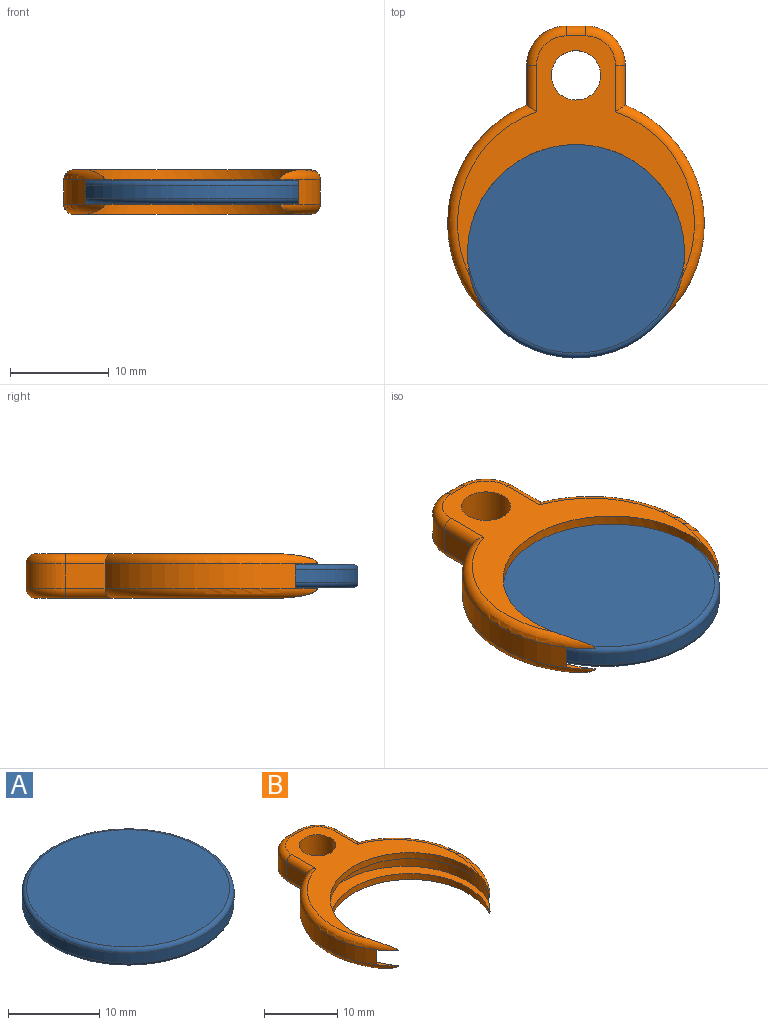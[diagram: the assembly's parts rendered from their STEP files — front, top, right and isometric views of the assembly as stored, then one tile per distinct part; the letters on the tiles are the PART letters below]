
ASSEMBLY  parts=2 mates=1
PART A: 277 faces, bbox 25.2x25.2x2.3 mm
  f0: plane 22.25x22.25mm, normal (0,0,-1), area 375.8mm2, adj f3,f5,f6,f7,f8,f23,f24,f25
  f1: cylinder r=11.62mm len=23.25mm, axis (0,0,-1), area 97.1mm2, adj f3,f4
  f2: plane 22.25x22.25mm, normal (0,0,1), area 388.8mm2, adj f4
  f3: torus R=11.12mm, axis (0,0,1), area 56.5mm2, adj f0,f1
  f4: torus R=11.12mm, axis (0,0,1), area 56.5mm2, adj f1,f2
  f5: plane 0.29x0.23mm, normal (0,-1,0), area 0.1mm2, adj f0,f6,f8,f9
  f6: plane 2.11x0.29mm, normal (-1,0,0), area 0.6mm2, adj f0,f5,f7,f9
  f7: plane 0.29x0.23mm, normal (0,1,0), area 0.1mm2, adj f0,f6,f8,f9
  f8: plane 2.11x0.29mm, normal (1,0,0), area 0.6mm2, adj f0,f5,f7,f9
  f9: plane 2.11x0.23mm, normal (0,0,-1), area 0.5mm2, adj f5,f6,f7,f8
  f10: extruded ~0.29x0.24mm, area 0.1mm2, adj f11,f53,f54,f273
  f11: extruded ~0.29x0.25mm, area 0.1mm2, adj f10,f12,f54,f273
  f12: extruded ~0.29x0.24mm, area 0.1mm2, adj f11,f13,f54,f273
  f13: extruded ~0.33x0.33mm, area 0.2mm2, adj f12,f14,f54,f273
  f14: extruded ~0.33x0.32mm, area 0.2mm2, adj f13,f53,f54,f273
  f15: extruded ~0.29x0.18mm, area 0.1mm2, adj f16,f51,f54,f55
  f16: extruded ~0.29x0.21mm, area 0.1mm2, adj f15,f17,f54,f55
  f17: extruded ~0.29x0.24mm, area 0.1mm2, adj f16,f18,f54,f55
  f18: plane 0.29x0.27mm, normal (0,-1,0), area 0.1mm2, adj f17,f19,f54,f55
  f19: extruded ~0.29x0.28mm, area 0.1mm2, adj f18,f20,f54,f55
  f20: extruded ~0.29x0.17mm, area 0.1mm2, adj f19,f21,f54,f55
  f21: extruded ~0.29x0.23mm, area 0.1mm2, adj f20,f22,f54,f55
  f22: extruded ~0.42x0.29mm, area 0.1mm2, adj f21,f51,f54,f55
  f23: plane 0.29x0.14mm, normal (-1,0,0), area 0mm2, adj f0,f24,f52,f54
  f24: plane 0.51x0.29mm, normal (0,1,0), area 0.2mm2, adj f0,f23,f25,f54
  f25: extruded ~0.29x0.21mm, area 0.1mm2, adj f0,f24,f26,f54
  f26: extruded ~0.41x0.29mm, area 0.1mm2, adj f0,f25,f27,f54
  f27: extruded ~0.38x0.29mm, area 0.1mm2, adj f0,f26,f28,f54
  f28: extruded ~0.29x0.26mm, area 0.1mm2, adj f0,f27,f29,f54
  f29: extruded ~0.29x0.19mm, area 0.1mm2, adj f0,f28,f30,f54
  f30: extruded ~0.29x0.14mm, area 0.1mm2, adj f0,f29,f31,f54
  f31: extruded ~0.29x0.14mm, area 0mm2, adj f0,f30,f32,f54
  f32: extruded ~0.29x0.13mm, area 0mm2, adj f0,f31,f33,f54
  f33: extruded ~0.29x0.1mm, area 0mm2, adj f0,f32,f34,f54
  f34: extruded ~0.29x0.24mm, area 0.1mm2, adj f0,f33,f35,f54
  f35: extruded ~0.29x0.23mm, area 0.1mm2, adj f0,f34,f36,f54
  f36: extruded ~0.31x0.29mm, area 0.1mm2, adj f0,f35,f37,f54
  f37: extruded ~0.45x0.29mm, area 0.1mm2, adj f0,f36,f38,f54
  f38: extruded ~0.58x0.29mm, area 0.2mm2, adj f0,f37,f39,f54
  f39: extruded ~0.38x0.29mm, area 0.1mm2, adj f0,f38,f40,f54
  f40: extruded ~0.3x0.29mm, area 0.1mm2, adj f0,f39,f41,f54
  f41: extruded ~0.37x0.29mm, area 0.1mm2, adj f0,f40,f42,f54
  f42: plane 0.29x0.26mm, normal (0,1,0), area 0.1mm2, adj f0,f41,f43,f54
  f43: extruded ~0.29x0.17mm, area 0.1mm2, adj f0,f42,f44,f54
  f44: extruded ~0.29x0.09mm, area 0mm2, adj f0,f43,f45,f54
  f45: extruded ~0.29x0.19mm, area 0.1mm2, adj f0,f44,f46,f54
  f46: extruded ~0.29x0.12mm, area 0mm2, adj f0,f45,f47,f54
  f47: extruded ~0.41x0.29mm, area 0.1mm2, adj f0,f46,f48,f54
  f48: extruded ~0.35x0.29mm, area 0.1mm2, adj f0,f47,f49,f54
  f49: extruded ~0.29x0.17mm, area 0.1mm2, adj f0,f48,f50,f54
  f50: extruded ~0.29x0.12mm, area 0mm2, adj f0,f49,f52,f54
  f51: extruded ~0.29x0.29mm, area 0.1mm2, adj f15,f22,f54,f55
  f52: plane 0.29x0.28mm, normal (-0.12,-0.99,0), area 0.1mm2, adj f0,f23,f50,f54
  f53: extruded ~0.29x0.25mm, area 0.1mm2, adj f10,f14,f54,f273
  f54: plane 2.18x1.4mm, normal (0,0,-1), area 1.3mm2, adj f10,f11,f12,f13,f14,f15,f16,f17
  f55: plane 0.95x0.53mm, normal (0,0,-1), area 0.4mm2, adj f15,f16,f17,f18,f19,f20,f21,f22
  f56: extruded ~0.33x0.29mm, area 0.1mm2, adj f57,f82,f83,f274
  f57: extruded ~0.29x0.21mm, area 0.1mm2, adj f56,f58,f83,f274
  f58: extruded ~0.29x0.19mm, area 0.1mm2, adj f57,f59,f83,f274
  f59: extruded ~0.29x0.23mm, area 0.1mm2, adj f58,f60,f83,f274
  f60: extruded ~0.39x0.29mm, area 0.1mm2, adj f59,f61,f83,f274
  f61: plane 0.29x0.23mm, normal (-0.04,-1,0), area 0.1mm2, adj f60,f62,f83,f274
  f62: plane 0.29x0.13mm, normal (1,0,0), area 0mm2, adj f61,f82,f83,f274
  f63: plane 0.29x0.21mm, normal (0.98,-0.21,0), area 0.1mm2, adj f0,f64,f81,f83
  f64: plane 0.29x0.17mm, normal (0,-1,0), area 0mm2, adj f0,f63,f65,f83
  f65: plane 1.01x0.29mm, normal (-1,0,0), area 0.3mm2, adj f0,f64,f66,f83
  f66: extruded ~0.38x0.29mm, area 0.1mm2, adj f0,f65,f67,f83
  f67: extruded ~0.39x0.29mm, area 0.1mm2, adj f0,f66,f68,f83
  f68: extruded ~0.29x0.26mm, area 0.1mm2, adj f0,f67,f69,f83
  f69: extruded ~0.29x0.24mm, area 0.1mm2, adj f0,f68,f70,f83
  f70: plane 0.29x0.17mm, normal (0.93,-0.37,0), area 0.1mm2, adj f0,f69,f71,f83
  f71: extruded ~0.42x0.29mm, area 0.1mm2, adj f0,f70,f72,f83
  f72: extruded ~0.29x0.24mm, area 0.1mm2, adj f0,f71,f73,f83
  f73: extruded ~0.29x0.26mm, area 0.1mm2, adj f0,f72,f74,f83
  f74: plane 0.29x0.09mm, normal (1,0,0), area 0mm2, adj f0,f73,f75,f83
  f75: plane 0.29x0.25mm, normal (0.03,1,0), area 0.1mm2, adj f0,f74,f76,f83
  f76: extruded ~0.72x0.47mm, area 0.3mm2, adj f0,f75,f77,f83
  f77: extruded ~0.32x0.29mm, area 0.1mm2, adj f0,f76,f78,f83
  f78: extruded ~0.35x0.29mm, area 0.1mm2, adj f0,f77,f79,f83
  f79: extruded ~0.29x0.28mm, area 0.1mm2, adj f0,f78,f80,f83
  f80: extruded ~0.29x0.22mm, area 0.1mm2, adj f0,f79,f81,f83
  f81: plane 0.29x0.01mm, normal (0,-1,0), area 0mm2, adj f0,f63,f80,f83
  f82: extruded ~0.32x0.29mm, area 0.1mm2, adj f56,f62,f83,f274
  f83: plane 1.54x1.19mm, normal (0,0,-1), area 0.9mm2, adj f56,f57,f58,f59,f60,f61,f62,f63
  f84: extruded ~0.33x0.29mm, area 0.1mm2, adj f85,f106,f107,f275
  f85: extruded ~0.31x0.29mm, area 0.1mm2, adj f84,f86,f107,f275
  f86: extruded ~0.43x0.29mm, area 0.1mm2, adj f85,f87,f107,f275
  f87: extruded ~0.43x0.29mm, area 0.1mm2, adj f86,f88,f107,f275
  f88: extruded ~0.31x0.29mm, area 0.1mm2, adj f87,f89,f107,f275
  f89: extruded ~0.34x0.29mm, area 0.1mm2, adj f88,f90,f107,f275
  f90: extruded ~0.45x0.29mm, area 0.1mm2, adj f89,f106,f107,f275
  f91: extruded ~0.46x0.29mm, area 0.2mm2, adj f0,f92,f105,f107
  f92: extruded ~0.47x0.29mm, area 0.2mm2, adj f0,f91,f93,f107
  f93: plane 0.29x0.01mm, normal (0,1,0), area 0mm2, adj f0,f92,f94,f107
  f94: extruded ~0.31x0.29mm, area 0.1mm2, adj f0,f93,f95,f107
  f95: plane 0.51x0.29mm, normal (-1,0,0), area 0.2mm2, adj f0,f94,f96,f107
  f96: plane 0.29x0.23mm, normal (0,1,0), area 0.1mm2, adj f0,f95,f97,f107
  f97: plane 2.11x0.29mm, normal (1,0,0), area 0.6mm2, adj f0,f96,f98,f107
  f98: plane 0.29x0.16mm, normal (0,-1,0), area 0mm2, adj f0,f97,f99,f107
  f99: plane 0.29x0.19mm, normal (-0.97,-0.24,0), area 0.1mm2, adj f0,f98,f100,f107
  f100: plane 0.29x0.02mm, normal (0,-1,0), area 0mm2, adj f0,f99,f101,f107
  f101: extruded ~0.29x0.2mm, area 0.1mm2, adj f0,f100,f102,f107
  f102: extruded ~0.29x0.27mm, area 0.1mm2, adj f0,f101,f103,f107
  f103: extruded ~0.45x0.29mm, area 0.2mm2, adj f0,f102,f104,f107
  f104: extruded ~0.57x0.29mm, area 0.2mm2, adj f0,f103,f105,f107
  f105: extruded ~0.57x0.29mm, area 0.2mm2, adj f0,f91,f104,f107
  f106: extruded ~0.45x0.29mm, area 0.1mm2, adj f84,f90,f107,f275
  f107: plane 2.14x1.31mm, normal (0,0,-1), area 1.1mm2, adj f84,f85,f86,f87,f88,f89,f90,f91
  f108: plane 0.61x0.29mm, normal (0.94,-0.35,0), area 0.2mm2, adj f109,f120,f121,f276
  f109: plane 0.64x0.29mm, normal (0,1,0), area 0.2mm2, adj f108,f110,f121,f276
  f110: plane 0.61x0.29mm, normal (-0.94,-0.35,0), area 0.2mm2, adj f109,f111,f121,f276
  f111: extruded ~0.29x0.29mm, area 0.1mm2, adj f110,f120,f121,f276
  f112: plane 0.63x0.29mm, normal (0.93,-0.36,0), area 0.2mm2, adj f0,f113,f119,f121
  f113: plane 0.29x0.24mm, normal (0,-1,0), area 0.1mm2, adj f0,f112,f114,f121
  f114: plane 1.99x0.78mm, normal (-0.93,0.36,0), area 0.6mm2, adj f0,f113,f115,f121
  f115: plane 0.29x0.19mm, normal (0,1,0), area 0.1mm2, adj f0,f114,f116,f121
  f116: plane 1.99x0.78mm, normal (0.93,0.37,0), area 0.6mm2, adj f0,f115,f117,f121
  f117: plane 0.29x0.23mm, normal (0,-1,0), area 0.1mm2, adj f0,f116,f118,f121
  f118: plane 0.63x0.29mm, normal (-0.93,-0.36,0), area 0.2mm2, adj f0,f117,f119,f121
  f119: plane 0.79x0.29mm, normal (0,-1,0), area 0.2mm2, adj f0,f112,f118,f121
  f120: extruded ~0.29x0.29mm, area 0.1mm2, adj f108,f111,f121,f276
  f121: plane 1.99x1.76mm, normal (0,0,-1), area 1mm2, adj f108,f109,f110,f111,f112,f113,f114,f115
  f122: plane 0.97x0.29mm, normal (1,0,0), area 0.3mm2, adj f0,f123,f149,f150
  f123: plane 0.29x0.23mm, normal (0,-1,0), area 0.1mm2, adj f0,f122,f124,f150
  f124: plane 0.97x0.29mm, normal (-1,0,0), area 0.3mm2, adj f0,f123,f125,f150
  f125: extruded ~0.41x0.29mm, area 0.1mm2, adj f0,f124,f126,f150
  f126: extruded ~0.38x0.29mm, area 0.1mm2, adj f0,f125,f127,f150
  f127: extruded ~0.29x0.29mm, area 0.1mm2, adj f0,f126,f128,f150
  f128: extruded ~0.29x0.19mm, area 0.1mm2, adj f0,f127,f129,f150
  f129: plane 0.29x0.01mm, normal (0,1,0), area 0mm2, adj f0,f128,f130,f150
  f130: extruded ~0.46x0.29mm, area 0.2mm2, adj f0,f129,f131,f150
  f131: extruded ~0.29x0.26mm, area 0.1mm2, adj f0,f130,f132,f150
  f132: extruded ~0.29x0.18mm, area 0.1mm2, adj f0,f131,f133,f150
  f133: plane 0.29x0.01mm, normal (0,1,0), area 0mm2, adj f0,f132,f134,f150
  f134: plane 0.29x0.2mm, normal (-0.98,0.18,0), area 0.1mm2, adj f0,f133,f135,f150
  f135: plane 0.29x0.18mm, normal (0,1,0), area 0.1mm2, adj f0,f134,f136,f150
  f136: plane 1.49x0.29mm, normal (1,0,0), area 0.4mm2, adj f0,f135,f137,f150
  f137: plane 0.29x0.23mm, normal (0,-1,0), area 0.1mm2, adj f0,f136,f138,f150
  f138: plane 0.78x0.29mm, normal (-1,0,0), area 0.2mm2, adj f0,f137,f139,f150
  f139: extruded ~0.42x0.29mm, area 0.1mm2, adj f0,f138,f140,f150
  f140: extruded ~0.31x0.29mm, area 0.1mm2, adj f0,f139,f141,f150
  f141: extruded ~0.29x0.24mm, area 0.1mm2, adj f0,f140,f142,f150
  f142: extruded ~0.29x0.27mm, area 0.1mm2, adj f0,f141,f143,f150
  f143: plane 0.97x0.29mm, normal (1,0,0), area 0.3mm2, adj f0,f142,f144,f150
  f144: plane 0.29x0.23mm, normal (0,-1,0), area 0.1mm2, adj f0,f143,f145,f150
  f145: plane 0.83x0.29mm, normal (-1,0,0), area 0.2mm2, adj f0,f144,f146,f150
  f146: extruded ~0.37x0.29mm, area 0.1mm2, adj f0,f145,f147,f150
  f147: extruded ~0.31x0.29mm, area 0.1mm2, adj f0,f146,f148,f150
  f148: extruded ~0.29x0.24mm, area 0.1mm2, adj f0,f147,f149,f150
  f149: extruded ~0.29x0.27mm, area 0.1mm2, adj f0,f122,f148,f150
  f150: plane 2.12x1.51mm, normal (0,0,-1), area 1.3mm2, adj f122,f123,f124,f125,f126,f127,f128,f129
  f151: plane 0.96x0.29mm, normal (-1,0,0), area 0.3mm2, adj f0,f152,f167,f168
  f152: plane 0.29x0.23mm, normal (0,1,0), area 0.1mm2, adj f0,f151,f153,f168
  f153: plane 0.97x0.29mm, normal (1,0,0), area 0.3mm2, adj f0,f152,f154,f168
  f154: extruded ~0.41x0.29mm, area 0.1mm2, adj f0,f153,f155,f168
  f155: extruded ~0.41x0.29mm, area 0.1mm2, adj f0,f154,f156,f168
  f156: extruded ~0.29x0.28mm, area 0.1mm2, adj f0,f155,f157,f168
  f157: extruded ~0.29x0.19mm, area 0.1mm2, adj f0,f156,f158,f168
  f158: plane 0.29x0.01mm, normal (0,-1,0), area 0mm2, adj f0,f157,f159,f168
  f159: plane 0.29x0.2mm, normal (0.99,-0.16,0), area 0.1mm2, adj f0,f158,f160,f168
  f160: plane 0.29x0.19mm, normal (0,-1,0), area 0.1mm2, adj f0,f159,f161,f168
  f161: plane 1.49x0.29mm, normal (-1,0,0), area 0.4mm2, adj f0,f160,f162,f168
  f162: plane 0.29x0.23mm, normal (0,1,0), area 0.1mm2, adj f0,f161,f163,f168
  f163: plane 0.78x0.29mm, normal (1,0,0), area 0.2mm2, adj f0,f162,f164,f168
  f164: extruded ~0.42x0.29mm, area 0.1mm2, adj f0,f163,f165,f168
  f165: extruded ~0.34x0.29mm, area 0.1mm2, adj f0,f164,f166,f168
  f166: extruded ~0.29x0.26mm, area 0.1mm2, adj f0,f165,f167,f168
  f167: extruded ~0.29x0.27mm, area 0.1mm2, adj f0,f151,f166,f168
  f168: plane 1.51x1.24mm, normal (0,0,-1), area 0.8mm2, adj f151,f152,f153,f154,f155,f156,f157,f158
  f169: extruded ~0.29x0.11mm, area 0mm2, adj f0,f170,f176,f177
  f170: extruded ~0.29x0.11mm, area 0mm2, adj f0,f169,f171,f177
  f171: extruded ~0.29x0.1mm, area 0mm2, adj f0,f170,f172,f177
  f172: extruded ~0.29x0.09mm, area 0mm2, adj f0,f171,f173,f177
  f173: extruded ~0.29x0.11mm, area 0mm2, adj f0,f172,f174,f177
  f174: extruded ~0.29x0.11mm, area 0mm2, adj f0,f173,f175,f177
  f175: extruded ~0.29x0.09mm, area 0mm2, adj f0,f174,f176,f177
  f176: extruded ~0.29x0.1mm, area 0mm2, adj f0,f169,f175,f177
  f177: plane 0.3x0.27mm, normal (0,0,-1), area 0.1mm2, adj f169,f170,f171,f172,f173,f174,f175,f176
  f178: plane 0.29x0.23mm, normal (0,-1,0), area 0.1mm2, adj f0,f179,f181,f182
  f179: plane 1.49x0.29mm, normal (-1,0,0), area 0.4mm2, adj f0,f178,f180,f182
  f180: plane 0.29x0.23mm, normal (0,1,0), area 0.1mm2, adj f0,f179,f181,f182
  f181: plane 1.49x0.29mm, normal (1,0,0), area 0.4mm2, adj f0,f178,f180,f182
  f182: plane 1.49x0.23mm, normal (0,0,-1), area 0.3mm2, adj f178,f179,f180,f181
  f183: extruded ~0.32x0.29mm, area 0.1mm2, adj f0,f184,f207,f208
  f184: extruded ~0.29x0.25mm, area 0.1mm2, adj f0,f183,f185,f208
  f185: extruded ~0.36x0.29mm, area 0.1mm2, adj f0,f184,f186,f208
  f186: extruded ~0.29x0.26mm, area 0.1mm2, adj f0,f185,f187,f208
  f187: extruded ~0.29x0.1mm, area 0mm2, adj f0,f186,f188,f208
  f188: extruded ~0.29x0.1mm, area 0mm2, adj f0,f187,f189,f208
  f189: extruded ~0.29x0.14mm, area 0mm2, adj f0,f188,f190,f208
  f190: extruded ~0.29x0.24mm, area 0.1mm2, adj f0,f189,f191,f208
  f191: extruded ~0.41x0.29mm, area 0.1mm2, adj f0,f190,f192,f208
  f192: plane 0.29x0.18mm, normal (-0.92,-0.4,0), area 0.1mm2, adj f0,f191,f193,f208
  f193: extruded ~0.47x0.29mm, area 0.1mm2, adj f0,f192,f194,f208
  f194: extruded ~0.41x0.29mm, area 0.1mm2, adj f0,f193,f195,f208
  f195: extruded ~0.29x0.29mm, area 0.1mm2, adj f0,f194,f196,f208
  f196: extruded ~0.29x0.17mm, area 0.1mm2, adj f0,f195,f197,f208
  f197: extruded ~0.29x0.13mm, area 0.1mm2, adj f0,f196,f198,f208
  f198: extruded ~0.3x0.29mm, area 0.1mm2, adj f0,f197,f199,f208
  f199: extruded ~0.29x0.29mm, area 0.1mm2, adj f0,f198,f200,f208
  f200: extruded ~0.29x0.15mm, area 0.1mm2, adj f0,f199,f201,f208
  f201: extruded ~0.29x0.17mm, area 0.1mm2, adj f0,f200,f202,f208
  f202: extruded ~0.29x0.27mm, area 0.1mm2, adj f0,f201,f203,f208
  f203: extruded ~0.29x0.24mm, area 0.1mm2, adj f0,f202,f204,f208
  f204: extruded ~0.29x0.23mm, area 0.1mm2, adj f0,f203,f205,f208
  f205: plane 0.29x0.21mm, normal (1,0,0), area 0.1mm2, adj f0,f204,f206,f208
  f206: extruded ~0.46x0.29mm, area 0.1mm2, adj f0,f205,f207,f208
  f207: extruded ~0.43x0.29mm, area 0.1mm2, adj f0,f183,f206,f208
  f208: plane 1.54x1.05mm, normal (0,0,-1), area 0.7mm2, adj f183,f184,f185,f186,f187,f188,f189,f190
  f209: plane 0.96x0.29mm, normal (1,0,0), area 0.3mm2, adj f0,f210,f225,f226
  f210: plane 0.29x0.23mm, normal (0,-1,0), area 0.1mm2, adj f0,f209,f211,f226
  f211: plane 0.97x0.29mm, normal (-1,0,0), area 0.3mm2, adj f0,f210,f212,f226
  f212: extruded ~0.41x0.29mm, area 0.1mm2, adj f0,f211,f213,f226
  f213: extruded ~0.4x0.29mm, area 0.1mm2, adj f0,f212,f214,f226
  f214: extruded ~0.29x0.28mm, area 0.1mm2, adj f0,f213,f215,f226
  f215: extruded ~0.29x0.19mm, area 0.1mm2, adj f0,f214,f216,f226
  f216: plane 0.29x0.01mm, normal (0,1,0), area 0mm2, adj f0,f215,f217,f226
  f217: plane 0.29x0.2mm, normal (-0.98,0.18,0), area 0.1mm2, adj f0,f216,f218,f226
  f218: plane 0.29x0.18mm, normal (0,1,0), area 0.1mm2, adj f0,f217,f219,f226
  f219: plane 1.49x0.29mm, normal (1,0,0), area 0.4mm2, adj f0,f218,f220,f226
  f220: plane 0.29x0.23mm, normal (0,-1,0), area 0.1mm2, adj f0,f219,f221,f226
  f221: plane 0.78x0.29mm, normal (-1,0,0), area 0.2mm2, adj f0,f220,f222,f226
  f222: extruded ~0.42x0.29mm, area 0.1mm2, adj f0,f221,f223,f226
  f223: extruded ~0.34x0.29mm, area 0.1mm2, adj f0,f222,f224,f226
  f224: extruded ~0.29x0.26mm, area 0.1mm2, adj f0,f223,f225,f226
  f225: extruded ~0.29x0.27mm, area 0.1mm2, adj f0,f209,f224,f226
  f226: plane 1.51x1.24mm, normal (0,0,-1), area 0.8mm2, adj f209,f210,f211,f212,f213,f214,f215,f216
  f227: plane 0.97x0.29mm, normal (1,0,0), area 0.3mm2, adj f0,f228,f254,f255
  f228: plane 0.29x0.23mm, normal (0,-1,0), area 0.1mm2, adj f0,f227,f229,f255
  f229: plane 0.97x0.29mm, normal (-1,0,0), area 0.3mm2, adj f0,f228,f230,f255
  f230: extruded ~0.41x0.29mm, area 0.1mm2, adj f0,f229,f231,f255
  f231: extruded ~0.38x0.29mm, area 0.1mm2, adj f0,f230,f232,f255
  f232: extruded ~0.29x0.29mm, area 0.1mm2, adj f0,f231,f233,f255
  f233: extruded ~0.29x0.19mm, area 0.1mm2, adj f0,f232,f234,f255
  f234: plane 0.29x0.01mm, normal (0,1,0), area 0mm2, adj f0,f233,f235,f255
  f235: extruded ~0.46x0.29mm, area 0.2mm2, adj f0,f234,f236,f255
  f236: extruded ~0.29x0.26mm, area 0.1mm2, adj f0,f235,f237,f255
  f237: extruded ~0.29x0.18mm, area 0.1mm2, adj f0,f236,f238,f255
  f238: plane 0.29x0.01mm, normal (0,1,0), area 0mm2, adj f0,f237,f239,f255
  f239: plane 0.29x0.2mm, normal (-0.98,0.18,0), area 0.1mm2, adj f0,f238,f240,f255
  f240: plane 0.29x0.18mm, normal (0,1,0), area 0.1mm2, adj f0,f239,f241,f255
  f241: plane 1.49x0.29mm, normal (1,0,0), area 0.4mm2, adj f0,f240,f242,f255
  f242: plane 0.29x0.23mm, normal (0,-1,0), area 0.1mm2, adj f0,f241,f243,f255
  f243: plane 0.78x0.29mm, normal (-1,0,0), area 0.2mm2, adj f0,f242,f244,f255
  f244: extruded ~0.42x0.29mm, area 0.1mm2, adj f0,f243,f245,f255
  f245: extruded ~0.31x0.29mm, area 0.1mm2, adj f0,f244,f246,f255
  f246: extruded ~0.29x0.24mm, area 0.1mm2, adj f0,f245,f247,f255
  f247: extruded ~0.29x0.27mm, area 0.1mm2, adj f0,f246,f248,f255
  f248: plane 0.97x0.29mm, normal (1,0,0), area 0.3mm2, adj f0,f247,f249,f255
  f249: plane 0.29x0.23mm, normal (0,-1,0), area 0.1mm2, adj f0,f248,f250,f255
  f250: plane 0.83x0.29mm, normal (-1,0,0), area 0.2mm2, adj f0,f249,f251,f255
  f251: extruded ~0.37x0.29mm, area 0.1mm2, adj f0,f250,f252,f255
  f252: extruded ~0.31x0.29mm, area 0.1mm2, adj f0,f251,f253,f255
  f253: extruded ~0.29x0.24mm, area 0.1mm2, adj f0,f252,f254,f255
  f254: extruded ~0.29x0.27mm, area 0.1mm2, adj f0,f227,f253,f255
  f255: plane 2.12x1.51mm, normal (0,0,-1), area 1.3mm2, adj f227,f228,f229,f230,f231,f232,f233,f234
  f256: plane 0.29x0.24mm, normal (0,1,0), area 0.1mm2, adj f0,f257,f271,f272
  f257: plane 1.49x0.6mm, normal (0.93,-0.37,0), area 0.5mm2, adj f0,f256,f258,f272
  f258: plane 0.29x0.21mm, normal (0.93,0.37,0), area 0.1mm2, adj f0,f257,f259,f272
  f259: extruded ~0.33x0.29mm, area 0.1mm2, adj f0,f258,f260,f272
  f260: extruded ~0.29x0.17mm, area 0mm2, adj f0,f259,f261,f272
  f261: plane 0.29x0.18mm, normal (1,0,0), area 0.1mm2, adj f0,f260,f262,f272
  f262: extruded ~0.29x0.2mm, area 0.1mm2, adj f0,f261,f263,f272
  f263: extruded ~0.31x0.29mm, area 0.1mm2, adj f0,f262,f264,f272
  f264: extruded ~0.36x0.29mm, area 0.1mm2, adj f0,f263,f265,f272
  f265: plane 1.69x0.64mm, normal (-0.94,-0.35,0), area 0.5mm2, adj f0,f264,f266,f272
  f266: plane 0.29x0.24mm, normal (0,1,0), area 0.1mm2, adj f0,f265,f267,f272
  f267: extruded ~1.03x0.37mm, area 0.3mm2, adj f0,f266,f268,f272
  f268: extruded ~0.29x0.24mm, area 0.1mm2, adj f0,f267,f269,f272
  f269: plane 0.29x0.01mm, normal (0,1,0), area 0mm2, adj f0,f268,f270,f272
  f270: extruded ~0.42x0.29mm, area 0.1mm2, adj f0,f269,f271,f272
  f271: plane 0.85x0.33mm, normal (-0.93,0.36,0), area 0.3mm2, adj f0,f256,f270,f272
  f272: plane 2.15x1.39mm, normal (0,0,-1), area 0.9mm2, adj f256,f257,f258,f259,f260,f261,f262,f263
  f273: plane 0.66x0.66mm, normal (0,0,-1), area 0.4mm2, adj f10,f11,f12,f13,f14,f53
  f274: plane 0.73x0.57mm, normal (0,0,-1), area 0.3mm2, adj f56,f57,f58,f59,f60,f61,f62,f82
  f275: plane 1.16x0.85mm, normal (0,0,-1), area 0.8mm2, adj f84,f85,f86,f87,f88,f89,f90,f106
  f276: plane 0.9x0.64mm, normal (0,0,-1), area 0.3mm2, adj f108,f109,f110,f111,f120
PART B: 29 faces, bbox 28.1x30.6x4.5 mm
  f0: cylinder r=13mm len=19.25mm, axis (0,0,-1), area 57.4mm2, adj f1,f11,f19,f22
  f1: plane 4x2.5mm, normal (-1,0,0), area 10mm2, adj f0,f8,f21,f23
  f2: cylinder r=13mm len=19.25mm, axis (0,0,-1), area 57.4mm2, adj f3,f11,f15,f26
  f3: plane 4x2.5mm, normal (1,0,0), area 10mm2, adj f2,f7,f16,f28
  f4: plane 2.5x2mm, normal (0,1,0), area 5mm2, adj f7,f8,f18,f25
  f5: plane 24.33x24mm, normal (0,0,1), area 143.1mm2, adj f9,f10,f15,f16,f17,f18,f19,f20
  f6: plane 24.33x24mm, normal (0,0,-1), area 143.1mm2, adj f9,f14,f22,f23,f24,f25,f26,f27
  f7: cylinder r=4mm len=4mm, axis (0,0,1), area 15.7mm2, adj f3,f4,f17,f27
  f8: cylinder r=4mm len=4mm, axis (0,0,-1), area 15.7mm2, adj f1,f4,f20,f24
  f9: cylinder r=2.5mm len=5mm, axis (0,0,1), area 70.7mm2, adj f5,f6
  f10: cylinder r=11mm len=22mm, axis (0,0,1), area 46.3mm2, adj f5,f13,f15,f19
  f11: cylinder r=12mm len=24mm, axis (0,0,1), area 121.4mm2, adj f0,f2,f12,f13
  f12: plane 24x19.5mm, normal (0,0,1), area 68.4mm2, adj f11,f14,f22,f26
  f13: plane 24x19.5mm, normal (0,0,-1), area 68.4mm2, adj f10,f11,f15,f19
  f14: cylinder r=11mm len=22mm, axis (0,0,1), area 46.3mm2, adj f6,f12,f22,f26
  f15: torus R=12mm, axis (0,0,1), area 37.4mm2, adj f2,f5,f10,f13,f16
  f16: cylinder r=1mm len=4.69mm, axis (0,-1,0), area 6.7mm2, adj f3,f5,f15,f17
  f17: torus R=3mm, axis (0,0,1), area 9mm2, adj f5,f7,f16,f18
  f18: cylinder r=1mm len=2mm, axis (1,0,0), area 3.1mm2, adj f4,f5,f17,f20
  f19: torus R=12mm, axis (0,0,1), area 37.4mm2, adj f0,f5,f10,f13,f21
  f20: torus R=3mm, axis (0,0,1), area 9mm2, adj f5,f8,f18,f21
  f21: cylinder r=1mm len=4.69mm, axis (0,1,0), area 6.7mm2, adj f1,f5,f19,f20
  f22: torus R=12mm, axis (0,0,1), area 37.4mm2, adj f0,f6,f12,f14,f23
  f23: cylinder r=1mm len=4.69mm, axis (0,-1,0), area 6.7mm2, adj f1,f6,f22,f24
  f24: torus R=3mm, axis (0,0,1), area 9mm2, adj f6,f8,f23,f25
  f25: cylinder r=1mm len=2mm, axis (-1,0,0), area 3.1mm2, adj f4,f6,f24,f27
  f26: torus R=12mm, axis (0,0,1), area 37.4mm2, adj f2,f6,f12,f14,f28
  f27: torus R=3mm, axis (0,0,1), area 9mm2, adj f6,f7,f25,f28
  f28: cylinder r=1mm len=4.69mm, axis (0,1,0), area 6.7mm2, adj f3,f6,f26,f27
PLACE A t=(-10.28,-6.7,7.86)mm
PLACE B t=(-10.28,-4.7,6.77)mm
MATE revolute A.f1 <-> B.f11  axis (0,0,-1) through (-10.28,-6.7,9.02)mm
